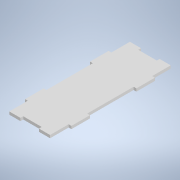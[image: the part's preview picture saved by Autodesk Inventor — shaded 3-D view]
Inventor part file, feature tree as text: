
AUTODESK INVENTOR PART (.ipt)
format: ipt  version: 2020.3 (Build 243373000, 373)  size: 148,480 bytes
history: native  units: mm
features: extrude x2, sketch x2
ambient origin geometry x8: Origin, YZ Plane, XZ Plane, XY Plane, X Axis, Y Axis, Z Axis, Center Point
bodies: Solid1 (feature_tree)
feature tree (4):
  extrude  "Base"  Depth=50.0mm
  extrude  "Tabs"  Depth=20.0mm
  sketch  "Sketch1"  dims[d0=130.0mm d1=50.0mm]
  sketch  "Sketch2"  dims[d2=3.0mm d3=0.0mm d10=20.0mm d11=20.0mm d12=20.0mm d13=20.0mm d14=50.0mm d15=3.0mm d16=0.0mm d17=0.0mm d19=10.0mm d20=3.0mm]
